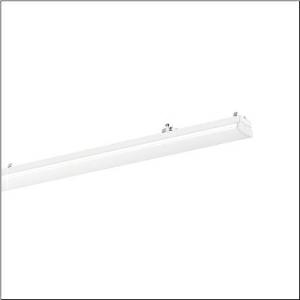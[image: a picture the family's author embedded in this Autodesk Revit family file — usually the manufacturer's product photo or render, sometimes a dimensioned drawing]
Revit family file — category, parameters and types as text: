
# Revit family: licross_11_recessed_opal_ho_51te1ddn46xm
name_source: partatom
category: Lighting Fixtures
units: mm (PartAtom-declared; Revit-internal decimal feet)

## family parameters
Cut with Voids When Loaded = No
Host = Face
Light Source = No
Part Type = Normal
Room Calculation Point = No
Round Connector Dimension = Use Diameter
Shared = No

## types (1)
- --- (1 x LED, 6320 lm, 33.5 W, 4000K)
    Apparent Load = 34 VA
    CIE Flux Codes = 44 73 91 87 100
    Color Rendering = 80
    Color Temperature = 4000K
    Default Elevation = 1800 mm
    Description = Licross 11 recessed opal HO, luminaire insert, of sheet steel, coil coated, white, length: 1.500mm, width: 76mm, height: 87mm, LED rated luminous flux: 6.320lm, light colour: 840, SDCM (Standard Deviation of Colour Matching)MacAdam ≤ 2 SDCM (initial), control gear: DALI 2, with plug, 5-pole, with phase selection, mains connection: 220..240V, AC, 50/60Hz, rated input power: 34W, internal wiring halogen-free, primary optical cover: cover, of PMMA, light emission: direct with ceiling illumination distribution, primary light characteristic: symmetric, protection rating (complete): IP54, insulation class (complete): insulation class I (protective earthing), certification: CE, ENEC, VDE, UKCA, protection symbol: D if used in an environment with non-conductive dust loads with corresponding accessories, impact resistance: IK06, permissible ambient temperature for indoor applications: -25..+45°C, corresponds to IFS (International Featured Standards) requirements for safety and quality in the food industry, reducing of maximum allowable ambient temperature of 5°C with ceiling mounting, LABS conformity tested according to VDMA 24364:2018-05, The light source and the operating device comply with the requirements of the Ecodesign Regulation (EU) 2019/2020 and are replaceable in accordance with this regulation, packaging unit: 1 piece
    Height = 83 mm
    Lamp = 1 x LED
    Lamp Light Flux = 6320 lm
    Lamp Power = 33.5 W
    Lamp count = 1
    Length = 1500 mm
    Luminous efficacy = 189 lm/W
    Manufacturer = Siteco
    ModVariant = No
    Model = 51TE1DDN46XM
    Mounting Place = Ceiling
    Mounting Type = Pendant
    Number of Poles = 1
    OnlyDefault = Yes
    Power Factor = 1
    Product Name = Licross 11 recessed opal HO
    Product group = luminaire insert | ceiling pendant
    ProductGroupID = 901
    Protection Class = Protection class I
    Protection Degree = IP 54
    RLX_Detail_Level = 1
    RLX_Emergency_Light_Flux = 0 lm
    RLX_Emergency_Type = 0
    RLX_Emergency_Type_DB = No
    RlxData = <blob elided: 27117 chars, md5=54adc20b>
    Socket = socket
    Standby Power = 0 W
    System Light Flux = 6320 lm
    System Power = 34 W
    Type Comments = factory setting: luminous flux: 100 % | dim-lin: 254 | 232 mA
    Type Image = l_1313666.jpg
    URL = http://relux.com
    VarID = @adj_083647
    Voltage = 0 V
    Weight = 0.00 kg
    Width = 76 mm

## geometry (parser evidence)
native form markers: Blend x4, Sweep x13
no freeform markers — native parametric forms only
